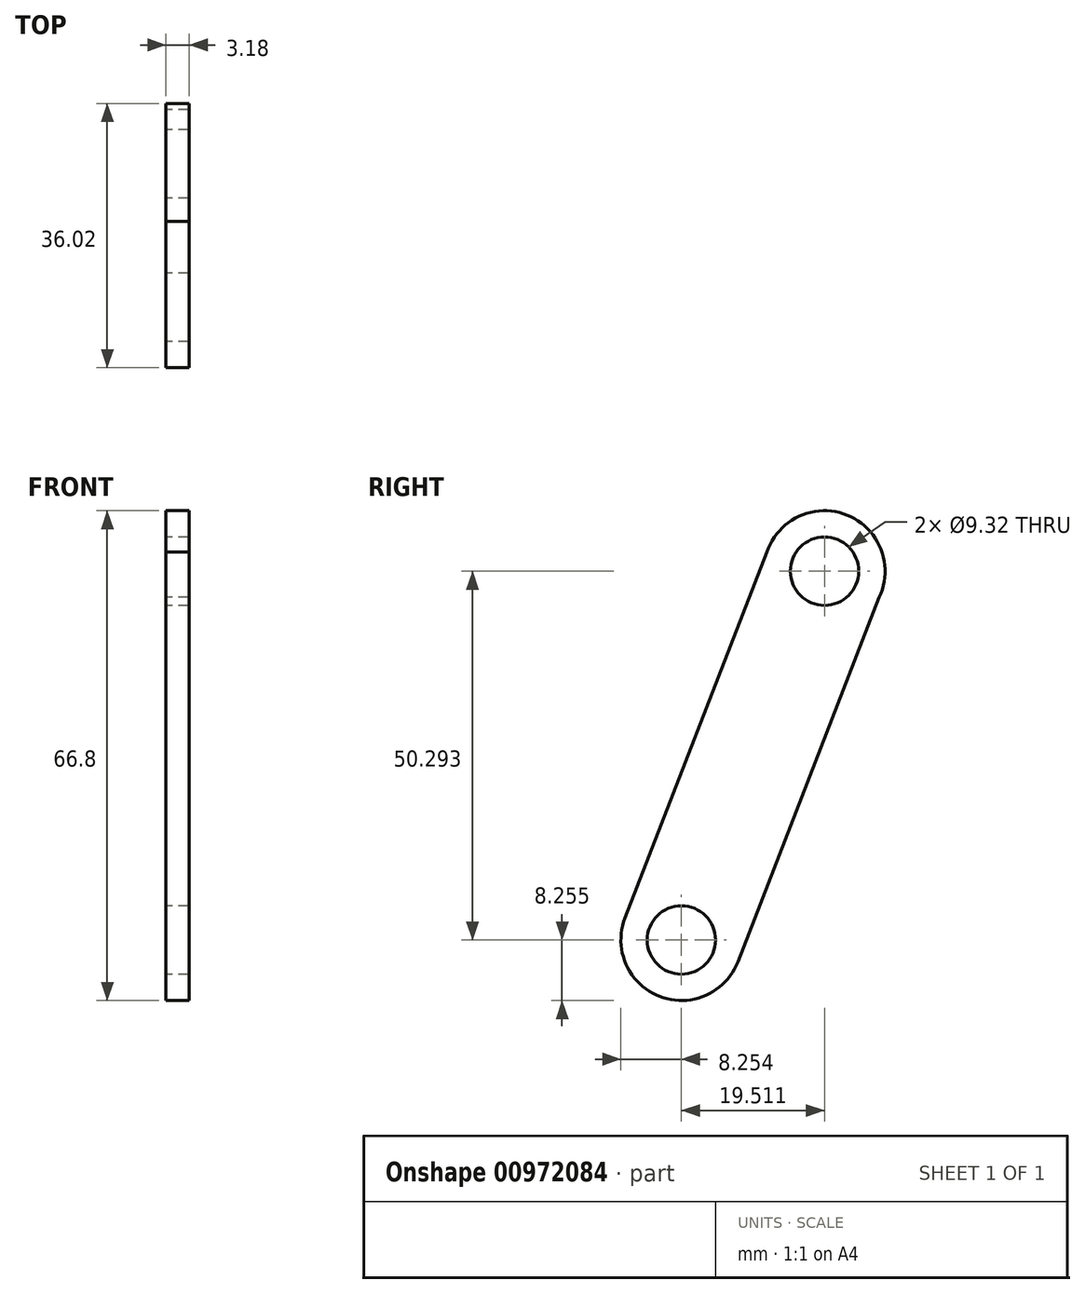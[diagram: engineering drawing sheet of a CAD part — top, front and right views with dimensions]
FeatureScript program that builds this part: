
annotation { "Feature Type Name" : "Feature", "Feature Type Description" : "" }
export const myFeature = defineFeature(function(context is Context, id is Id, definition is map)
    precondition{}
    {
        {
            var Q0;
            Q0=qCreatedBy(makeId("Right.planeOp"),FACE);
            var sketch = newSketch(context, id + "F0", { "sketchPlane" : qUnion([Q0])});
            skCircle(sketch, "E0", {"center": v(-21.1, -19.64) * mm, "radius": 4.66 * mm});
            skCircle(sketch, "E1", {"center": v(-21.1, -19.64) * mm, "radius": 8.26 * mm});
            skCircle(sketch, "E2", {"center": v(-40.6, -69.94) * mm, "radius": 4.66 * mm});
            skCircle(sketch, "E3", {"center": v(-40.6, -69.94) * mm, "radius": 8.26 * mm});
            skLineSegment(sketch, "E4", {"start": v(-28.62, -16.26) * mm, "end": v(-48.3, -66.95) * mm});
            skLineSegment(sketch, "E5", {"start": v(-13.2, -22.02) * mm, "end": v(-32.9, -72.92) * mm});
            skSolve(sketch);
        }
        {
            var Q0;
            Q0 = qSketchRegion(id + "F0", true);
            extrude(context, id + "F1", {"entities" : qUnion([Q0]), "depth" : 3.17 * mm, "offsetDistance" : 25.4 * mm});
        }
    });
